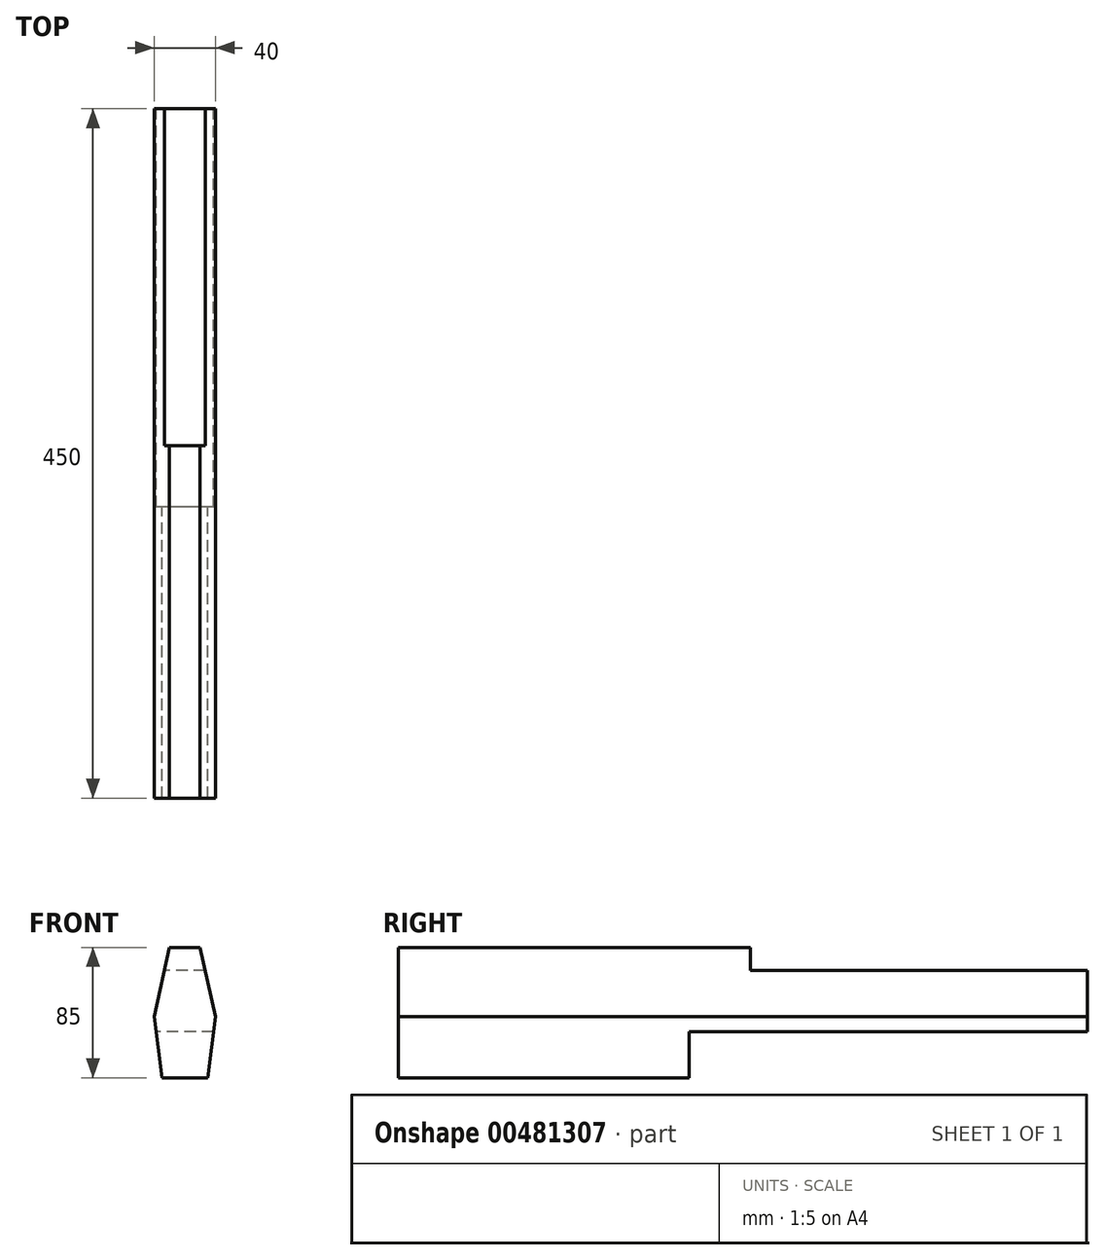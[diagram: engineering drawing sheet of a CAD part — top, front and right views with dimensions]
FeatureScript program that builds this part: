
annotation { "Feature Type Name" : "Feature", "Feature Type Description" : "" }
export const myFeature = defineFeature(function(context is Context, id is Id, definition is map)
    precondition{}
    {
        {
            var Q0;
            Q0=qCreatedBy(makeId("Front.planeOp"),FACE);
            var sketch = newSketch(context, id + "F0", { "sketchPlane" : qUnion([Q0])});
            skLineSegment(sketch, "E0", {"start": v(-10, 45) * mm, "end": v(10, 45) * mm});
            skLineSegment(sketch, "E1", {"start": v(10, 45) * mm, "end": v(20, 0) * mm});
            skLineSegment(sketch, "E2", {"start": v(20, 0) * mm, "end": v(15, -40) * mm});
            skLineSegment(sketch, "E3", {"start": v(15, -40) * mm, "end": v(-15, -40) * mm});
            skLineSegment(sketch, "E4", {"start": v(-15, -40) * mm, "end": v(-20, 0) * mm});
            skLineSegment(sketch, "E5", {"start": v(-20, 0) * mm, "end": v(-10, 45) * mm});
            skSolve(sketch);
        }
        {
            var Q0;
            Q0=makeQuery(id+"F0.imprint","IMPRINT",FACE,{"disambiguationData":[TD([[makeQuery(id+"F0.imprint","IMPRINT",EDGE,{"derivedFrom":sQuery(id+"F0.wireOp",EDGE,"E0")}),-1.0]])]});
            extrude(context, id + "F1", {"entities" : qUnion([Q0]), "depth" : 450 * mm});
        }
        {
            var Q0;
            Q0=makeQuery(id+"F1.opExtrude","CAP_FACE",FACE,{"disambiguationData":[OSD([sQuery(id+"F0.wireOp",EDGE,"E0"),sQuery(id+"F0.wireOp",EDGE,"E1"),sQuery(id+"F0.wireOp",EDGE,"E2"),sQuery(id+"F0.wireOp",EDGE,"E3"),sQuery(id+"F0.wireOp",EDGE,"E4"),sQuery(id+"F0.wireOp",EDGE,"E5")])],"isStart":true});
            var sketch = newSketch(context, id + "F2", { "sketchPlane" : qUnion([Q0])});
            skLineSegment(sketch, "E6.bottom", {"start": v(-16.75, 30) * mm, "end": v(23.25, 30) * mm});
            skLineSegment(sketch, "E6.top", {"start": v(-16.75, 45) * mm, "end": v(23.25, 45) * mm});
            skLineSegment(sketch, "E6.left", {"start": v(-16.75, 30) * mm, "end": v(-16.75, 45) * mm});
            skLineSegment(sketch, "E6.right", {"start": v(23.25, 30) * mm, "end": v(23.25, 45) * mm});
            skSolve(sketch);
        }
        {
            var Q0;
            {var subQ0=sQuery(id+"F2.wireOp",EDGE,"E6.bottom");var subQ1=makeQuery(id+"F1.opExtrude","CAP_EDGE",EDGE,{"disambiguationData":[OSD([sQuery(id+"F0.wireOp",EDGE,"E1")])],"isStart":true});var subQ2=makeQuery(id+"F2.imprint","INTERSECT",VERTEX,{"derivedFrom":[subQ1,subQ0]});Q0=makeQuery(id+"F2.imprint","IMPRINT",FACE,{"disambiguationData":[TD([[makeQuery(id+"F2.imprint","IMPRINT",EDGE,{"disambiguationData":[TD([[subQ2,-1.0]])],"derivedFrom":subQ0}),1.0]])]});}
            extrude(context, id + "F3", {"entities" : qUnion([Q0]), "operationType" : NewBodyOperationType.REMOVE, "oppositeDirection" : true, "depth" : 220 * mm});
        }
        {
            var Q0;
            Q0=makeQuery(id+"F1.opExtrude","CAP_FACE",FACE,{"disambiguationData":[OSD([sQuery(id+"F0.wireOp",EDGE,"E0"),sQuery(id+"F0.wireOp",EDGE,"E1"),sQuery(id+"F0.wireOp",EDGE,"E2"),sQuery(id+"F0.wireOp",EDGE,"E3"),sQuery(id+"F0.wireOp",EDGE,"E4"),sQuery(id+"F0.wireOp",EDGE,"E5")])],"isStart":true});
            var sketch = newSketch(context, id + "F4", { "sketchPlane" : qUnion([Q0])});
            skLineSegment(sketch, "E7.bottom", {"start": v(-34.72, -50.6) * mm, "end": v(38, -50.6) * mm});
            skLineSegment(sketch, "E7.top", {"start": v(-34.72, -10) * mm, "end": v(38, -10) * mm});
            skLineSegment(sketch, "E7.left", {"start": v(-34.72, -50.6) * mm, "end": v(-34.72, -10) * mm});
            skLineSegment(sketch, "E7.right", {"start": v(38, -50.6) * mm, "end": v(38, -10) * mm});
            skSolve(sketch);
        }
        {
            var Q0;
            {var subQ5=makeQuery(id+"F1.opExtrude","CAP_EDGE",EDGE,{"disambiguationData":[OSD([sQuery(id+"F0.wireOp",EDGE,"E3")])],"isStart":true});Q0=makeQuery(id+"F4.imprint","IMPRINT",FACE,{"disambiguationData":[TD([[makeQuery(id+"F4.imprint","IMPRINT",EDGE,{"derivedFrom":subQ5}),1.0]])]});}
            extrude(context, id + "F5", {"entities" : qUnion([Q0]), "operationType" : NewBodyOperationType.REMOVE, "oppositeDirection" : true, "depth" : 260 * mm});
        }
    });
